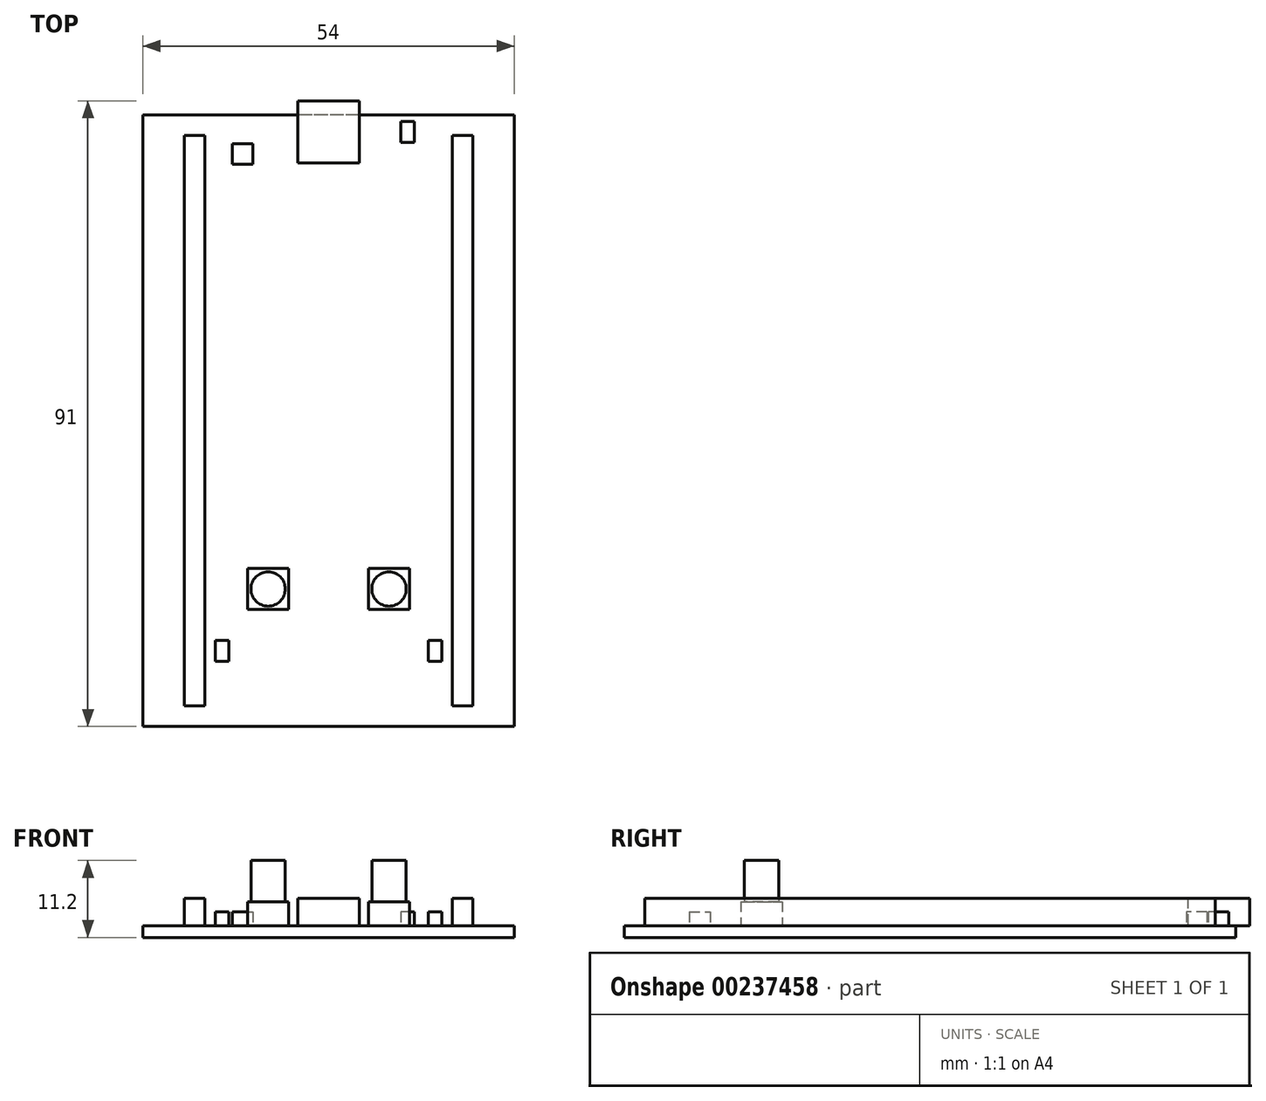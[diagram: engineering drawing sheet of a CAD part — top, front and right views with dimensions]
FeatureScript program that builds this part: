
annotation { "Feature Type Name" : "Feature", "Feature Type Description" : "" }
export const myFeature = defineFeature(function(context is Context, id is Id, definition is map)
    precondition{}
    {
        {
            var Q0;
            Q0=qCreatedBy(makeId("Top.planeOp"),FACE);
            var sketch = newSketch(context, id + "F0", { "sketchPlane" : qUnion([Q0])});
            skLineSegment(sketch, "E0", {"start": v(0, 0) * mm, "end": v(54, 0) * mm});
            skLineSegment(sketch, "E1", {"start": v(54, 0) * mm, "end": v(54, 89) * mm});
            skLineSegment(sketch, "E2", {"start": v(54, 89) * mm, "end": v(0, 89) * mm});
            skLineSegment(sketch, "E3", {"start": v(0, 89) * mm, "end": v(0, 0) * mm});
            skSolve(sketch);
        }
        {
            var Q0;
            Q0 = qSketchRegion(id + "F0", true);
            extrude(context, id + "F1", {"entities" : qUnion([Q0]), "depth" : 1.7 * mm});
        }
        {
            var Q0;
            Q0=makeQuery(id+"F1.opExtrude","CAP_FACE",FACE,{"disambiguationData":[OSD([sQuery(id+"F0.wireOp",EDGE,"E0"),sQuery(id+"F0.wireOp",EDGE,"E1"),sQuery(id+"F0.wireOp",EDGE,"E2"),sQuery(id+"F0.wireOp",EDGE,"E3")])],"isStart":false});
            var sketch = newSketch(context, id + "F2", { "sketchPlane" : qUnion([Q0])});
            skLineSegment(sketch, "E4", {"start": v(0, 0) * mm, "end": v(6, 0) * mm, "construction": true});
            skLineSegment(sketch, "E5", {"start": v(6, 0) * mm, "end": v(6, 3) * mm, "construction": true});
            skLineSegment(sketch, "E6", {"start": v(0, 89) * mm, "end": v(9, 89) * mm, "construction": true});
            skLineSegment(sketch, "E7", {"start": v(9, 89) * mm, "end": v(9, 86) * mm, "construction": true});
            skLineSegment(sketch, "E8", {"start": v(54, 89) * mm, "end": v(45, 89) * mm, "construction": true});
            skLineSegment(sketch, "E9", {"start": v(45, 89) * mm, "end": v(45, 86) * mm, "construction": true});
            skLineSegment(sketch, "E10", {"start": v(54, 0) * mm, "end": v(48, 0) * mm, "construction": true});
            skLineSegment(sketch, "E11", {"start": v(48, 0) * mm, "end": v(48, 3) * mm, "construction": true});
            skLineSegment(sketch, "E12.bottom", {"start": v(9, 86) * mm, "end": v(6, 86) * mm});
            skLineSegment(sketch, "E12.top", {"start": v(9, 3) * mm, "end": v(6, 3) * mm});
            skLineSegment(sketch, "E12.left", {"start": v(9, 86) * mm, "end": v(9, 3) * mm});
            skLineSegment(sketch, "E12.right", {"start": v(6, 86) * mm, "end": v(6, 3) * mm});
            skLineSegment(sketch, "E13.bottom", {"start": v(48, 3) * mm, "end": v(45, 3) * mm});
            skLineSegment(sketch, "E13.top", {"start": v(48, 86) * mm, "end": v(45, 86) * mm});
            skLineSegment(sketch, "E13.left", {"start": v(48, 3) * mm, "end": v(48, 86) * mm});
            skLineSegment(sketch, "E13.right", {"start": v(45, 3) * mm, "end": v(45, 86) * mm});
            skSolve(sketch);
        }
        {
            var Q0;
            Q0 = qSketchRegion(id + "F2", true);
            extrude(context, id + "F3", {"entities" : qUnion([Q0]), "operationType" : NewBodyOperationType.ADD, "depth" : 4 * mm});
        }
        {
            var Q0;
            Q0=makeQuery(id+"F1.opExtrude","CAP_FACE",FACE,{"disambiguationData":[OSD([sQuery(id+"F0.wireOp",EDGE,"E0"),sQuery(id+"F0.wireOp",EDGE,"E1"),sQuery(id+"F0.wireOp",EDGE,"E2"),sQuery(id+"F0.wireOp",EDGE,"E3")])],"isStart":false});
            var sketch = newSketch(context, id + "F4", { "sketchPlane" : qUnion([Q0])});
            skLineSegment(sketch, "E14", {"start": v(0, 0) * mm, "end": v(15.2, 0) * mm, "construction": true});
            skLineSegment(sketch, "E15", {"start": v(15.2, 0) * mm, "end": v(15.2, 17) * mm, "construction": true});
            skLineSegment(sketch, "E16", {"start": v(54, 0) * mm, "end": v(38.8, 0) * mm, "construction": true});
            skLineSegment(sketch, "E17", {"start": v(38.8, 0) * mm, "end": v(38.8, 17) * mm, "construction": true});
            skLineSegment(sketch, "E18.bottom", {"start": v(15.2, 17) * mm, "end": v(21.2, 17) * mm});
            skLineSegment(sketch, "E18.top", {"start": v(15.2, 23) * mm, "end": v(21.2, 23) * mm});
            skLineSegment(sketch, "E18.left", {"start": v(15.2, 17) * mm, "end": v(15.2, 23) * mm});
            skLineSegment(sketch, "E18.right", {"start": v(21.2, 17) * mm, "end": v(21.2, 23) * mm});
            skLineSegment(sketch, "E19.bottom", {"start": v(38.8, 17) * mm, "end": v(32.8, 17) * mm});
            skLineSegment(sketch, "E19.top", {"start": v(38.8, 23) * mm, "end": v(32.8, 23) * mm});
            skLineSegment(sketch, "E19.left", {"start": v(38.8, 17) * mm, "end": v(38.8, 23) * mm});
            skLineSegment(sketch, "E19.right", {"start": v(32.8, 17) * mm, "end": v(32.8, 23) * mm});
            skSolve(sketch);
        }
        {
            var Q0;
            Q0 = qSketchRegion(id + "F4", true);
            extrude(context, id + "F5", {"entities" : qUnion([Q0]), "operationType" : NewBodyOperationType.ADD, "depth" : 3.5 * mm});
        }
        {
            var Q0;
            Q0=makeQuery(id+"F5.opExtrude","CAP_FACE",FACE,{"disambiguationData":[OSD([sQuery(id+"F4.wireOp",EDGE,"E18.bottom"),sQuery(id+"F4.wireOp",EDGE,"E18.top"),sQuery(id+"F4.wireOp",EDGE,"E18.left"),sQuery(id+"F4.wireOp",EDGE,"E18.right")])],"isStart":false});
            var sketch = newSketch(context, id + "F6", { "sketchPlane" : qUnion([Q0])});
            skCircle(sketch, "E20", {"center": v(18.2, 20) * mm, "radius": 2.5 * mm});
            skPoint(sketch, "E20.centerSnap0", {"position": v(21.2, 20) * mm});
            skPoint(sketch, "E20.centerSnap1", {"position": v(18.2, 23) * mm});
            skSolve(sketch);
        }
        {
            var Q0;
            Q0=makeQuery(id+"F5.opExtrude","CAP_FACE",FACE,{"disambiguationData":[OSD([sQuery(id+"F4.wireOp",EDGE,"E19.bottom"),sQuery(id+"F4.wireOp",EDGE,"E19.top"),sQuery(id+"F4.wireOp",EDGE,"E19.left"),sQuery(id+"F4.wireOp",EDGE,"E19.right")])],"isStart":false});
            var sketch = newSketch(context, id + "F7", { "sketchPlane" : qUnion([Q0])});
            skCircle(sketch, "E21", {"center": v(35.8, 20) * mm, "radius": 2.5 * mm});
            skPoint(sketch, "E21.centerSnap0", {"position": v(35.8, 23) * mm});
            skPoint(sketch, "E21.centerSnap1", {"position": v(32.8, 20) * mm});
            skSolve(sketch);
        }
        {
            var Q0;
            Q0 = qSketchRegion(id + "F7", true);
            var Q1;
            Q1 = qSketchRegion(id + "F6", true);
            extrude(context, id + "F8", {"entities" : qUnion([Q0, Q1]), "operationType" : NewBodyOperationType.ADD, "depth" : 6 * mm});
        }
        {
            var Q0;
            Q0=makeQuery(id+"F1.opExtrude","CAP_FACE",FACE,{"disambiguationData":[OSD([sQuery(id+"F0.wireOp",EDGE,"E0"),sQuery(id+"F0.wireOp",EDGE,"E1"),sQuery(id+"F0.wireOp",EDGE,"E2"),sQuery(id+"F0.wireOp",EDGE,"E3")])],"isStart":false});
            var sketch = newSketch(context, id + "F9", { "sketchPlane" : qUnion([Q0])});
            skLineSegment(sketch, "E22", {"start": v(54, 0) * mm, "end": v(43.5, 0) * mm, "construction": true});
            skLineSegment(sketch, "E23", {"start": v(43.5, 0) * mm, "end": v(43.5, 9.5) * mm, "construction": true});
            skLineSegment(sketch, "E24", {"start": v(0, 0) * mm, "end": v(10.5, 0) * mm, "construction": true});
            skLineSegment(sketch, "E25", {"start": v(10.5, 0) * mm, "end": v(10.5, 9.5) * mm, "construction": true});
            skLineSegment(sketch, "E26.bottom", {"start": v(43.5, 9.5) * mm, "end": v(41.5, 9.5) * mm});
            skLineSegment(sketch, "E26.top", {"start": v(43.5, 12.5) * mm, "end": v(41.5, 12.5) * mm});
            skLineSegment(sketch, "E26.left", {"start": v(43.5, 9.5) * mm, "end": v(43.5, 12.5) * mm});
            skLineSegment(sketch, "E26.right", {"start": v(41.5, 9.5) * mm, "end": v(41.5, 12.5) * mm});
            skLineSegment(sketch, "E27.bottom", {"start": v(10.5, 9.5) * mm, "end": v(12.5, 9.5) * mm});
            skLineSegment(sketch, "E27.top", {"start": v(10.5, 12.5) * mm, "end": v(12.5, 12.5) * mm});
            skLineSegment(sketch, "E27.left", {"start": v(10.5, 9.5) * mm, "end": v(10.5, 12.5) * mm});
            skLineSegment(sketch, "E27.right", {"start": v(12.5, 9.5) * mm, "end": v(12.5, 12.5) * mm});
            skSolve(sketch);
        }
        {
            var Q0;
            Q0 = qSketchRegion(id + "F9", true);
            extrude(context, id + "F10", {"entities" : qUnion([Q0]), "operationType" : NewBodyOperationType.ADD, "depth" : 2 * mm});
        }
        {
            var Q0;
            Q0=makeQuery(id+"F1.opExtrude","CAP_FACE",FACE,{"disambiguationData":[OSD([sQuery(id+"F0.wireOp",EDGE,"E0"),sQuery(id+"F0.wireOp",EDGE,"E1"),sQuery(id+"F0.wireOp",EDGE,"E2"),sQuery(id+"F0.wireOp",EDGE,"E3")])],"isStart":false});
            var sketch = newSketch(context, id + "F11", { "sketchPlane" : qUnion([Q0])});
            skLineSegment(sketch, "E28", {"start": v(54, 89) * mm, "end": v(31.5, 89) * mm, "construction": true});
            skLineSegment(sketch, "E29", {"start": v(0, 89) * mm, "end": v(22.5, 89) * mm, "construction": true});
            skLineSegment(sketch, "E30", {"start": v(22.5, 89) * mm, "end": v(22.5, 91) * mm});
            skLineSegment(sketch, "E31", {"start": v(22.5, 91) * mm, "end": v(31.5, 91) * mm});
            skLineSegment(sketch, "E32", {"start": v(31.5, 91) * mm, "end": v(31.5, 82) * mm});
            skLineSegment(sketch, "E33", {"start": v(31.5, 82) * mm, "end": v(22.5, 82) * mm});
            skLineSegment(sketch, "E34", {"start": v(22.5, 82) * mm, "end": v(22.5, 89) * mm});
            skSolve(sketch);
        }
        {
            var Q0;
            {var subQ0=sQuery(id+"F11.wireOp",EDGE,"E33");Q0=makeQuery(id+"F11.imprint","IMPRINT",FACE,{"disambiguationData":[TD([[makeQuery(id+"F11.imprint","IMPRINT",EDGE,{"derivedFrom":subQ0}),-1.0]])]});}
            var Q1;
            {var subQ0=sQuery(id+"F11.wireOp",EDGE,"E30");Q1=makeQuery(id+"F11.imprint","IMPRINT",FACE,{"disambiguationData":[TD([[makeQuery(id+"F11.imprint","IMPRINT",EDGE,{"derivedFrom":subQ0}),-1.0]])]});}
            extrude(context, id + "F12", {"entities" : qUnion([Q0, Q1]), "operationType" : NewBodyOperationType.ADD, "depth" : 4 * mm});
        }
        {
            var Q0;
            Q0=makeQuery(id+"F1.opExtrude","CAP_FACE",FACE,{"disambiguationData":[OSD([sQuery(id+"F0.wireOp",EDGE,"E0"),sQuery(id+"F0.wireOp",EDGE,"E1"),sQuery(id+"F0.wireOp",EDGE,"E2"),sQuery(id+"F0.wireOp",EDGE,"E3")])],"isStart":false});
            var sketch = newSketch(context, id + "F13", { "sketchPlane" : qUnion([Q0])});
            skLineSegment(sketch, "E35", {"start": v(0, 89) * mm, "end": v(13, 89) * mm, "construction": true});
            skLineSegment(sketch, "E36", {"start": v(13, 89) * mm, "end": v(13, 84.8) * mm, "construction": true});
            skLineSegment(sketch, "E37.bottom", {"start": v(13, 84.8) * mm, "end": v(16, 84.8) * mm});
            skLineSegment(sketch, "E37.top", {"start": v(13, 81.8) * mm, "end": v(16, 81.8) * mm});
            skLineSegment(sketch, "E37.left", {"start": v(13, 84.8) * mm, "end": v(13, 81.8) * mm});
            skLineSegment(sketch, "E37.right", {"start": v(16, 84.8) * mm, "end": v(16, 81.8) * mm});
            skLineSegment(sketch, "E38", {"start": v(54, 89) * mm, "end": v(39.5, 89) * mm, "construction": true});
            skLineSegment(sketch, "E39", {"start": v(39.5, 89) * mm, "end": v(39.5, 88) * mm, "construction": true});
            skLineSegment(sketch, "E40.bottom", {"start": v(39.5, 88) * mm, "end": v(37.5, 88) * mm});
            skLineSegment(sketch, "E40.top", {"start": v(39.5, 85) * mm, "end": v(37.5, 85) * mm});
            skLineSegment(sketch, "E40.left", {"start": v(39.5, 88) * mm, "end": v(39.5, 85) * mm});
            skLineSegment(sketch, "E40.right", {"start": v(37.5, 88) * mm, "end": v(37.5, 85) * mm});
            skSolve(sketch);
        }
        {
            var Q0;
            Q0 = qSketchRegion(id + "F13", true);
            extrude(context, id + "F14", {"entities" : qUnion([Q0]), "operationType" : NewBodyOperationType.ADD, "depth" : 2 * mm});
        }
    });
